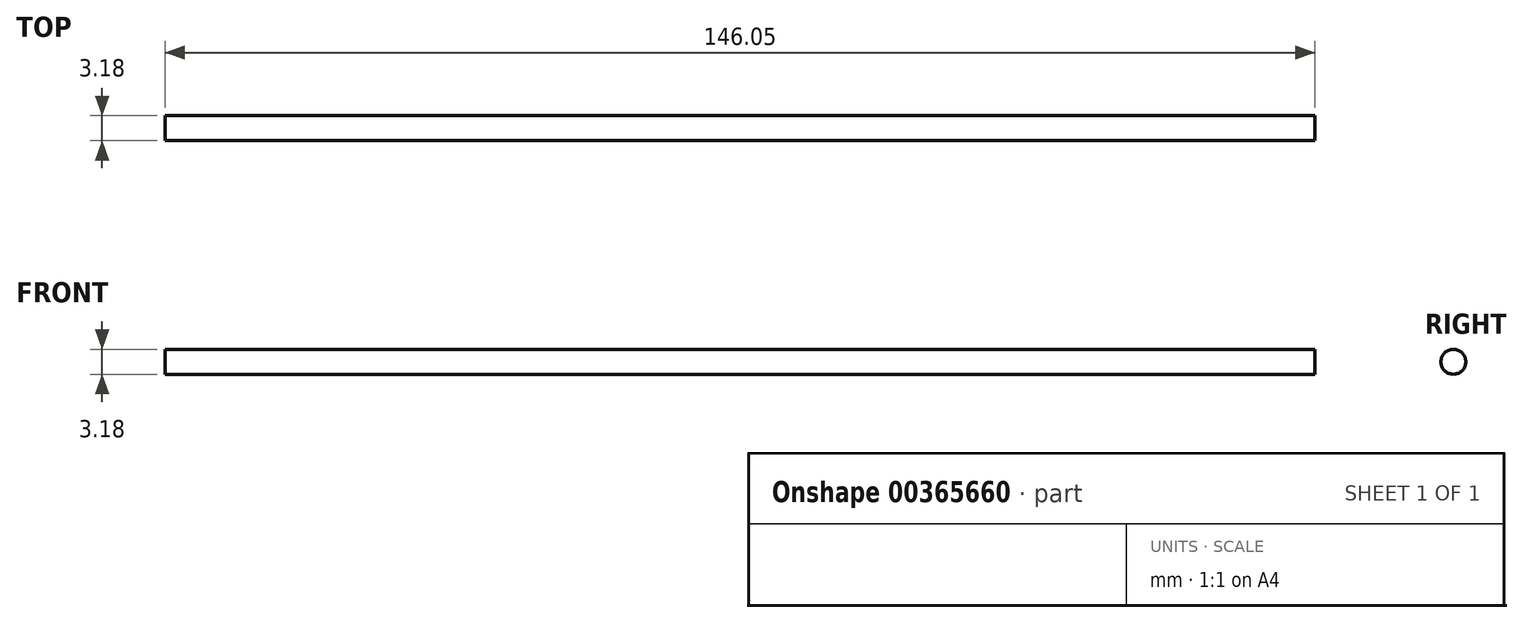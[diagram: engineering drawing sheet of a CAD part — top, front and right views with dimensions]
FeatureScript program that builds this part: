
annotation { "Feature Type Name" : "Feature", "Feature Type Description" : "" }
export const myFeature = defineFeature(function(context is Context, id is Id, definition is map)
    precondition{}
    {
        {
            var Q0;
            Q0=qCreatedBy(makeId("Front.planeOp"),FACE);
            var sketch = newSketch(context, id + "F0", { "sketchPlane" : qUnion([Q0])});
            skLineSegment(sketch, "E0.bottom", {"start": v(0, 0) * mm, "end": v(146.05, 0) * mm});
            skLineSegment(sketch, "E0.top", {"start": v(0, 1.59) * mm, "end": v(146.05, 1.59) * mm});
            skLineSegment(sketch, "E0.left", {"start": v(0, 0) * mm, "end": v(0, 1.59) * mm});
            skLineSegment(sketch, "E0.right", {"start": v(146.05, 0) * mm, "end": v(146.05, 1.59) * mm});
            skLineSegment(sketch, "E1", {"start": v(70, 0) * mm, "end": v(-31.22, 0) * mm, "construction": true});
            skSolve(sketch);
        }
        {
            var Q0;
            Q0 = qSketchRegion(id + "F0", true);
            var Q1;
            Q1=sQuery(id+"F0.wireOp",EDGE,"E1");
            revolve(context, id + "F1", {"entities" : qUnion([Q0]), "axis" : qUnion([Q1]), "revolveType" : RevolveType.FULL});
        }
    });
